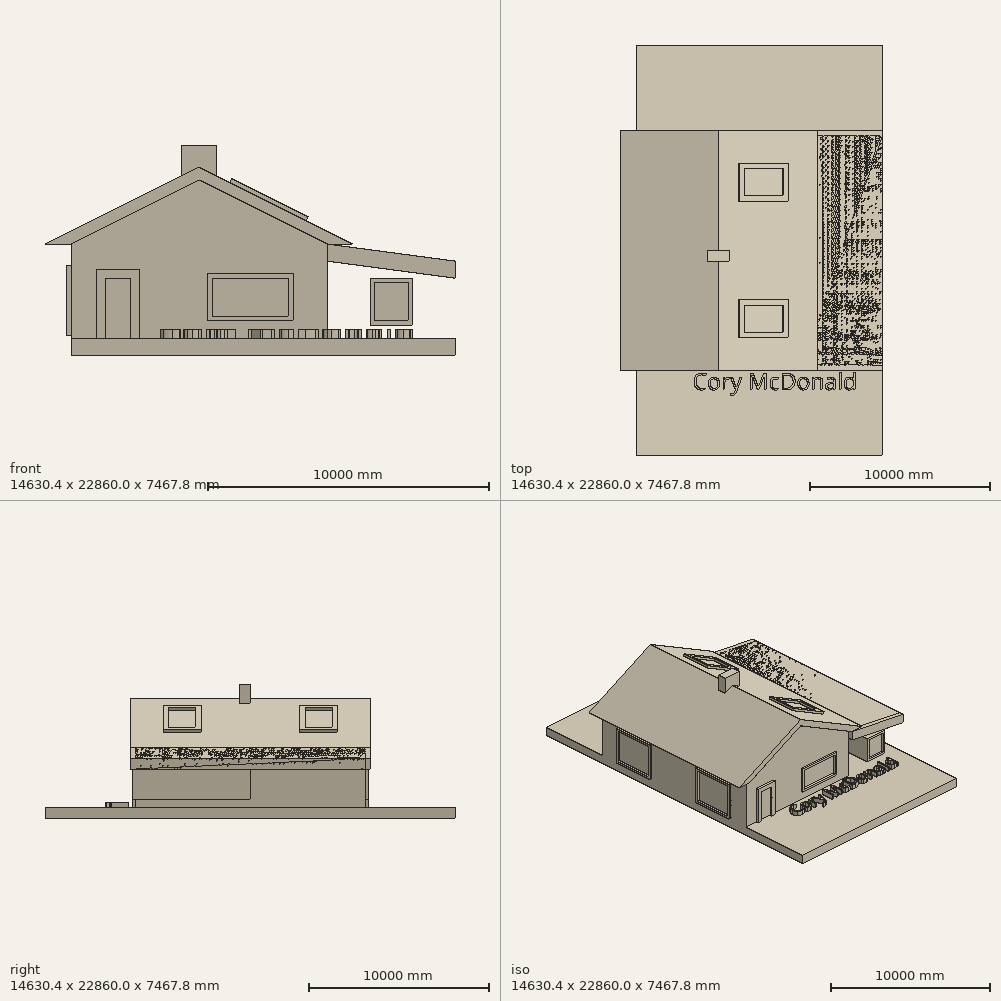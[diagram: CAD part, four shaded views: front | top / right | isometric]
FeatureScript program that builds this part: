
annotation { "Feature Type Name" : "Feature", "Feature Type Description" : "" }
export const myFeature = defineFeature(function(context is Context, id is Id, definition is map)
    precondition{}
    {
        {
            var Q0;
            Q0=qCreatedBy(makeId("Front.planeOp"),FACE);
            var sketch = newSketch(context, id + "F0", { "sketchPlane" : qUnion([Q0])});
            skLineSegment(sketch, "E0", {"start": v(0, 0) * mm, "end": v(-4572, 0) * mm});
            skLineSegment(sketch, "E1", {"start": v(0, 0) * mm, "end": v(4572, 0) * mm});
            skLineSegment(sketch, "E2", {"start": v(0, 0) * mm, "end": v(0, 2286) * mm});
            skLineSegment(sketch, "E3", {"start": v(0, 2286) * mm, "end": v(4572, 0) * mm});
            skLineSegment(sketch, "E4", {"start": v(0, 2286) * mm, "end": v(-4572, 0) * mm});
            skLineSegment(sketch, "E5", {"start": v(-4572, 0) * mm, "end": v(-5486.4, 0) * mm});
            skLineSegment(sketch, "E6", {"start": v(4572, 0) * mm, "end": v(5486.4, 0) * mm});
            skLineSegment(sketch, "E7", {"start": v(0, 2286) * mm, "end": v(0, 2743.2) * mm});
            skLineSegment(sketch, "E8", {"start": v(0, 2743.2) * mm, "end": v(-5486.4, 0) * mm});
            skLineSegment(sketch, "E9", {"start": v(0, 2743.2) * mm, "end": v(5486.4, 0) * mm});
            skLineSegment(sketch, "E10", {"start": v(-4572, 0) * mm, "end": v(-4572, -3352.8) * mm});
            skLineSegment(sketch, "E11", {"start": v(-4572, -3352.8) * mm, "end": v(4572, -3352.8) * mm});
            skLineSegment(sketch, "E12", {"start": v(4572, 0) * mm, "end": v(4572, -3352.8) * mm});
            skLineSegment(sketch, "E13", {"start": v(4572, -3352.8) * mm, "end": v(4572, -3962.4) * mm});
            skLineSegment(sketch, "E14", {"start": v(-4572, -3352.8) * mm, "end": v(-4572, -3962.4) * mm});
            skLineSegment(sketch, "E15", {"start": v(-4572, -3962.4) * mm, "end": v(4572, -3962.4) * mm});
            skLineSegment(sketch, "E16", {"start": v(4572, -3352.8) * mm, "end": v(9144, -3352.8) * mm});
            skLineSegment(sketch, "E17", {"start": v(4572, -3962.4) * mm, "end": v(9144, -3962.4) * mm});
            skLineSegment(sketch, "E18", {"start": v(9144, -3352.8) * mm, "end": v(9144, -3962.4) * mm});
            skLineSegment(sketch, "E19", {"start": v(9144, -3352.8) * mm, "end": v(9144, -609.6) * mm});
            skLineSegment(sketch, "E20", {"start": v(4572, 0) * mm, "end": v(9144, -609.6) * mm});
            skLineSegment(sketch, "E21", {"start": v(4572, 0) * mm, "end": v(4572, -609.6) * mm});
            skLineSegment(sketch, "E22", {"start": v(9144, -609.6) * mm, "end": v(9144, -1219.2) * mm});
            skLineSegment(sketch, "E23", {"start": v(9144, -1219.2) * mm, "end": v(4572, -609.6) * mm});
            skLineSegment(sketch, "E24", {"start": v(-3352.8, -3352.8) * mm, "end": v(-3352.8, -1219.2) * mm});
            skLineSegment(sketch, "E25", {"start": v(-3352.8, -1219.2) * mm, "end": v(-2438.4, -1219.2) * mm});
            skLineSegment(sketch, "E26", {"start": v(-2438.4, -1219.2) * mm, "end": v(-2438.4, -3352.8) * mm});
            skLineSegment(sketch, "E27.0", {"start": v(-2133.6, -914.4) * mm, "end": v(-2133.6, -3352.8) * mm});
            skLineSegment(sketch, "E27.1", {"start": v(-3657.6, -914.4) * mm, "end": v(-2133.6, -914.4) * mm});
            skLineSegment(sketch, "E27.2", {"start": v(-3657.6, -3352.8) * mm, "end": v(-3657.6, -914.4) * mm});
            skLineSegment(sketch, "E28.bottom", {"start": v(457.2, -1219.2) * mm, "end": v(3200.4, -1219.2) * mm});
            skLineSegment(sketch, "E28.top", {"start": v(457.2, -2590.8) * mm, "end": v(3200.4, -2590.8) * mm});
            skLineSegment(sketch, "E28.left", {"start": v(457.2, -1219.2) * mm, "end": v(457.2, -2590.8) * mm});
            skLineSegment(sketch, "E28.right", {"start": v(3200.4, -1219.2) * mm, "end": v(3200.4, -2590.8) * mm});
            skLineSegment(sketch, "E29.0", {"start": v(304.8, -1066.8) * mm, "end": v(3352.8, -1066.8) * mm});
            skLineSegment(sketch, "E29.1", {"start": v(304.8, -1066.8) * mm, "end": v(304.8, -2743.2) * mm});
            skLineSegment(sketch, "E29.2", {"start": v(304.8, -2743.2) * mm, "end": v(3352.8, -2743.2) * mm});
            skLineSegment(sketch, "E29.3", {"start": v(3352.8, -1066.8) * mm, "end": v(3352.8, -2743.2) * mm});
            skLineSegment(sketch, "E30.bottom", {"start": v(7467.6, -1371.6) * mm, "end": v(6248.4, -1371.6) * mm});
            skLineSegment(sketch, "E30.top", {"start": v(7467.6, -2743.2) * mm, "end": v(6248.4, -2743.2) * mm});
            skLineSegment(sketch, "E30.left", {"start": v(7467.6, -1371.6) * mm, "end": v(7467.6, -2743.2) * mm});
            skLineSegment(sketch, "E30.right", {"start": v(6248.4, -1371.6) * mm, "end": v(6248.4, -2743.2) * mm});
            skLineSegment(sketch, "E31.0", {"start": v(7620, -1219.2) * mm, "end": v(6096, -1219.2) * mm});
            skLineSegment(sketch, "E31.1", {"start": v(7620, -1219.2) * mm, "end": v(7620, -2895.6) * mm});
            skLineSegment(sketch, "E31.2", {"start": v(7620, -2895.6) * mm, "end": v(6096, -2895.6) * mm});
            skLineSegment(sketch, "E31.3", {"start": v(6096, -1219.2) * mm, "end": v(6096, -2895.6) * mm});
            skLineSegment(sketch, "E32", {"start": v(616.03, 2435.19) * mm, "end": v(616.03, 3505.35) * mm});
            skLineSegment(sketch, "E33", {"start": v(616.03, 3505.35) * mm, "end": v(-641, 3505.35) * mm});
            skLineSegment(sketch, "E34", {"start": v(-641, 3505.35) * mm, "end": v(-641, 2422.7) * mm});
            skSolve(sketch);
        }
        {
            var Q0;
            Q0=makeQuery(id+"F0.imprint","IMPRINT",FACE,{"disambiguationData":[TD([[makeQuery(id+"F0.imprint","IMPRINT",EDGE,{"derivedFrom":sQuery(id+"F0.wireOp",EDGE,"E3")}),1.0]])]});
            var Q1;
            Q1=makeQuery(id+"F0.imprint","IMPRINT",FACE,{"disambiguationData":[TD([[makeQuery(id+"F0.imprint","IMPRINT",EDGE,{"derivedFrom":sQuery(id+"F0.wireOp",EDGE,"E4")}),-1.0]])]});
            var Q2;
            Q2=makeQuery(id+"F0.imprint","IMPRINT",FACE,{"disambiguationData":[TD([[makeQuery(id+"F0.imprint","IMPRINT",EDGE,{"derivedFrom":sQuery(id+"F0.wireOp",EDGE,"E20")}),-1.0]])]});
            extrude(context, id + "F1", {"entities" : qUnion([Q0, Q1, Q2]), "endBound" : BoundingType.SYMMETRIC, "depth" : 13411.2 * mm, "offsetDistance" : 30.48 * mm});
        }
        {
            var Q0;
            Q0=makeQuery(id+"F0.imprint","IMPRINT",FACE,{"disambiguationData":[TD([[makeQuery(id+"F0.imprint","IMPRINT",EDGE,{"derivedFrom":sQuery(id+"F0.wireOp",EDGE,"E0")}),-1.0]])]});
            var Q1;
            Q1=makeQuery(id+"F0.imprint","IMPRINT",FACE,{"disambiguationData":[TD([[makeQuery(id+"F0.imprint","IMPRINT",EDGE,{"derivedFrom":sQuery(id+"F0.wireOp",EDGE,"E1")}),1.0]])]});
            var Q2;
            Q2=makeQuery(id+"F0.imprint","IMPRINT",FACE,{"disambiguationData":[TD([[makeQuery(id+"F0.imprint","IMPRINT",EDGE,{"derivedFrom":sQuery(id+"F0.wireOp",EDGE,"E0")}),1.0]])]});
            var Q3;
            Q3=makeQuery(id+"F0.imprint","IMPRINT",FACE,{"disambiguationData":[TD([[makeQuery(id+"F0.imprint","IMPRINT",EDGE,{"derivedFrom":sQuery(id+"F0.wireOp",EDGE,"E12")}),1.0]])]});
            extrude(context, id + "F2", {"entities" : qUnion([Q0, Q1, Q2, Q3]), "endBound" : BoundingType.SYMMETRIC, "depth" : 12801.6 * mm, "offsetDistance" : 30.48 * mm});
        }
        {
            var Q0;
            Q0=makeQuery(id+"F0.imprint","IMPRINT",FACE,{"disambiguationData":[TD([[makeQuery(id+"F0.imprint","IMPRINT",EDGE,{"derivedFrom":sQuery(id+"F0.wireOp",EDGE,"E13")}),1.0]])]});
            var Q1;
            {var subQ6=sQuery(id+"F0.wireOp",EDGE,"E13");Q1=makeQuery(id+"F0.imprint","IMPRINT",FACE,{"disambiguationData":[TD([[makeQuery(id+"F0.imprint","IMPRINT",EDGE,{"derivedFrom":subQ6}),-1.0]])]});}
            extrude(context, id + "F3", {"entities" : qUnion([Q0, Q1]), "operationType" : NewBodyOperationType.ADD, "endBound" : BoundingType.SYMMETRIC, "depth" : 22860 * mm, "offsetDistance" : 30.48 * mm});
        }
        {
            var Q0;
            Q0=makeQuery(id+"F0.imprint","IMPRINT",FACE,{"disambiguationData":[TD([[makeQuery(id+"F0.imprint","IMPRINT",EDGE,{"derivedFrom":sQuery(id+"F0.wireOp",EDGE,"E30.bottom")}),1.0]])]});
            var Q1;
            Q1=makeQuery(id+"F0.imprint","IMPRINT",FACE,{"disambiguationData":[TD([[makeQuery(id+"F0.imprint","IMPRINT",EDGE,{"derivedFrom":sQuery(id+"F0.wireOp",EDGE,"E28.bottom")}),-1.0]])]});
            extrude(context, id + "F4", {"entities" : qUnion([Q0, Q1]), "depth" : 6400.8 * mm, "offsetDistance" : 30.48 * mm});
        }
        {
            var Q0;
            Q0=makeQuery(id+"F0.imprint","IMPRINT",FACE,{"disambiguationData":[TD([[makeQuery(id+"F0.imprint","IMPRINT",EDGE,{"derivedFrom":sQuery(id+"F0.wireOp",EDGE,"E28.bottom")}),1.0]])]});
            var Q1;
            Q1=makeQuery(id+"F0.imprint","IMPRINT",FACE,{"disambiguationData":[TD([[makeQuery(id+"F0.imprint","IMPRINT",EDGE,{"derivedFrom":sQuery(id+"F0.wireOp",EDGE,"E30.bottom")}),-1.0]])]});
            extrude(context, id + "F5", {"entities" : qUnion([Q0, Q1]), "depth" : 6553.2 * mm, "offsetDistance" : 30.48 * mm});
        }
        {
            var Q0;
            {var subQ0=sQuery(id+"F0.wireOp",EDGE,"E24");Q0=makeQuery(id+"F0.imprint","IMPRINT",FACE,{"disambiguationData":[TD([[makeQuery(id+"F0.imprint","IMPRINT",EDGE,{"derivedFrom":subQ0}),1.0]])]});}
            extrude(context, id + "F6", {"entities" : qUnion([Q0]), "operationType" : NewBodyOperationType.ADD, "endBound" : BoundingType.SYMMETRIC, "depth" : 13106.4 * mm, "offsetDistance" : 30.48 * mm});
        }
        {
            var Q0;
            {var subQ0=sQuery(id+"F0.wireOp",EDGE,"E24");Q0=makeQuery(id+"F0.imprint","IMPRINT",FACE,{"disambiguationData":[TD([[makeQuery(id+"F0.imprint","IMPRINT",EDGE,{"derivedFrom":subQ0}),-1.0]])]});}
            extrude(context, id + "F7", {"entities" : qUnion([Q0]), "operationType" : NewBodyOperationType.ADD, "endBound" : BoundingType.SYMMETRIC, "depth" : 12801.6 * mm, "offsetDistance" : 30.48 * mm});
        }
        {
            var Q0;
            Q0=makeQuery(id+"F2.opExtrude","CAP_FACE",FACE,{"disambiguationData":[OSD([sQuery(id+"F0.wireOp",EDGE,"E3"),sQuery(id+"F0.wireOp",EDGE,"E4"),sQuery(id+"F0.wireOp",EDGE,"E10"),sQuery(id+"F0.wireOp",EDGE,"E11"),sQuery(id+"F0.wireOp",EDGE,"E16"),sQuery(id+"F0.wireOp",EDGE,"E19"),sQuery(id+"F0.wireOp",EDGE,"E21"),sQuery(id+"F0.wireOp",EDGE,"E23"),sQuery(id+"F0.wireOp",EDGE,"E27.0"),sQuery(id+"F0.wireOp",EDGE,"E27.1"),sQuery(id+"F0.wireOp",EDGE,"E27.2"),sQuery(id+"F0.wireOp",EDGE,"E29.0"),sQuery(id+"F0.wireOp",EDGE,"E29.1"),sQuery(id+"F0.wireOp",EDGE,"E29.2"),sQuery(id+"F0.wireOp",EDGE,"E29.3"),sQuery(id+"F0.wireOp",EDGE,"E31.0"),sQuery(id+"F0.wireOp",EDGE,"E31.1"),sQuery(id+"F0.wireOp",EDGE,"E31.2"),sQuery(id+"F0.wireOp",EDGE,"E31.3")])],"isStart":true});
            var sketch = newSketch(context, id + "F8", { "sketchPlane" : qUnion([Q0])});
            skLineSegment(sketch, "E35.bottom", {"start": v(-7620, -1219.2) * mm, "end": v(-6096, -1219.2) * mm});
            skLineSegment(sketch, "E35.top", {"start": v(-7620, -2895.6) * mm, "end": v(-6096, -2895.6) * mm});
            skLineSegment(sketch, "E35.left", {"start": v(-7620, -1219.2) * mm, "end": v(-7620, -2895.6) * mm});
            skLineSegment(sketch, "E35.right", {"start": v(-6096, -1219.2) * mm, "end": v(-6096, -2895.6) * mm});
            skLineSegment(sketch, "E36.0", {"start": v(-7315.2, -1524) * mm, "end": v(-6400.8, -1524) * mm});
            skLineSegment(sketch, "E36.1", {"start": v(-7315.2, -1524) * mm, "end": v(-7315.2, -2590.8) * mm});
            skLineSegment(sketch, "E36.2", {"start": v(-7315.2, -2590.8) * mm, "end": v(-6400.8, -2590.8) * mm});
            skLineSegment(sketch, "E36.3", {"start": v(-6400.8, -1524) * mm, "end": v(-6400.8, -2590.8) * mm});
            skSolve(sketch);
        }
        {
            var Q0;
            Q0 = qSketchRegion(id + "F8", true);
            extrude(context, id + "F9", {"entities" : qUnion([Q0]), "oppositeDirection" : true, "depth" : -3.05 * mm, "offsetDistance" : 30.48 * mm});
        }
        {
            var Q0;
            Q0=makeQuery(id+"F4.opExtrude","CAP_FACE",FACE,{"disambiguationData":[OSD([sQuery(id+"F0.wireOp",EDGE,"E28.bottom"),sQuery(id+"F0.wireOp",EDGE,"E28.top"),sQuery(id+"F0.wireOp",EDGE,"E28.left"),sQuery(id+"F0.wireOp",EDGE,"E28.right")])],"isStart":true});
            extrude(context, id + "F10", {"entities" : qUnion([Q0]), "operationType" : NewBodyOperationType.ADD, "depth" : 6400.8 * mm, "offsetDistance" : 30.48 * mm});
        }
        {
            var Q0;
            Q0=makeQuery(id+"F5.opExtrude","CAP_FACE",FACE,{"disambiguationData":[OSD([sQuery(id+"F0.wireOp",EDGE,"E28.bottom"),sQuery(id+"F0.wireOp",EDGE,"E28.top"),sQuery(id+"F0.wireOp",EDGE,"E28.left"),sQuery(id+"F0.wireOp",EDGE,"E28.right"),sQuery(id+"F0.wireOp",EDGE,"E29.0"),sQuery(id+"F0.wireOp",EDGE,"E29.1"),sQuery(id+"F0.wireOp",EDGE,"E29.2"),sQuery(id+"F0.wireOp",EDGE,"E29.3")])],"isStart":true});
            extrude(context, id + "F11", {"entities" : qUnion([Q0]), "depth" : 6553.2 * mm, "offsetDistance" : 30.48 * mm});
        }
        {
            var Q0;
            Q0 = qSketchRegion(id + "F8", true);
            extrude(context, id + "F12", {"entities" : qUnion([Q0]), "operationType" : NewBodyOperationType.ADD, "depth" : 152.4 * mm, "offsetDistance" : 30.48 * mm});
        }
        {
            var Q0;
            Q0=makeQuery(id+"F8.imprint","IMPRINT",FACE,{"disambiguationData":[TD([[makeQuery(id+"F8.imprint","IMPRINT",EDGE,{"derivedFrom":sQuery(id+"F8.wireOp",EDGE,"E36.0")}),-1.0]])]});
            extrude(context, id + "F13", {"entities" : qUnion([Q0]), "operationType" : NewBodyOperationType.ADD, "depth" : 30.48 * mm, "offsetDistance" : 30.48 * mm});
        }
        {
            var Q0;
            Q0=makeQuery(id+"F1.opExtrude","SWEPT_FACE",FACE,{"disambiguationData":[OSD([sQuery(id+"F0.wireOp",EDGE,"E9")])]});
            var sketch = newSketch(context, id + "F14", { "sketchPlane" : qUnion([Q0])});
            skLineSegment(sketch, "E37.bottom", {"start": v(-7.6, -4876.8) * mm, "end": v(3040.4, -4876.8) * mm});
            skLineSegment(sketch, "E37.top", {"start": v(-7.6, -2743.2) * mm, "end": v(3040.4, -2743.2) * mm});
            skLineSegment(sketch, "E37.left", {"start": v(-7.6, -4876.8) * mm, "end": v(-7.6, -2743.2) * mm});
            skLineSegment(sketch, "E37.right", {"start": v(3040.4, -4876.8) * mm, "end": v(3040.4, -2743.2) * mm});
            skLineSegment(sketch, "E38.bottom", {"start": v(-7.6, 2743.2) * mm, "end": v(3040.4, 2743.2) * mm});
            skLineSegment(sketch, "E38.top", {"start": v(-7.6, 4876.8) * mm, "end": v(3040.4, 4876.8) * mm});
            skLineSegment(sketch, "E38.left", {"start": v(-7.6, 2743.2) * mm, "end": v(-7.6, 4876.8) * mm});
            skLineSegment(sketch, "E38.right", {"start": v(3040.4, 2743.2) * mm, "end": v(3040.4, 4876.8) * mm});
            skLineSegment(sketch, "E39.0", {"start": v(297.2, -3048) * mm, "end": v(2735.6, -3048) * mm});
            skLineSegment(sketch, "E39.1", {"start": v(297.2, -4572) * mm, "end": v(297.2, -3048) * mm});
            skLineSegment(sketch, "E39.2", {"start": v(297.2, -4572) * mm, "end": v(2735.6, -4572) * mm});
            skLineSegment(sketch, "E39.3", {"start": v(2735.6, -4572) * mm, "end": v(2735.6, -3048) * mm});
            skLineSegment(sketch, "E40.0", {"start": v(297.2, 3048) * mm, "end": v(297.2, 4572) * mm});
            skLineSegment(sketch, "E40.1", {"start": v(297.2, 3048) * mm, "end": v(2735.6, 3048) * mm});
            skLineSegment(sketch, "E40.2", {"start": v(2735.6, 3048) * mm, "end": v(2735.6, 4572) * mm});
            skLineSegment(sketch, "E40.3", {"start": v(297.2, 4572) * mm, "end": v(2735.6, 4572) * mm});
            skSolve(sketch);
        }
        {
            var Q0;
            Q0=makeQuery(id+"F14.imprint","IMPRINT",FACE,{"disambiguationData":[TD([[makeQuery(id+"F14.imprint","IMPRINT",EDGE,{"derivedFrom":sQuery(id+"F14.wireOp",EDGE,"E38.bottom")}),1.0]])]});
            var Q1;
            Q1=makeQuery(id+"F14.imprint","IMPRINT",FACE,{"disambiguationData":[TD([[makeQuery(id+"F14.imprint","IMPRINT",EDGE,{"derivedFrom":sQuery(id+"F14.wireOp",EDGE,"E37.bottom")}),1.0]])]});
            extrude(context, id + "F15", {"entities" : qUnion([Q0, Q1]), "operationType" : NewBodyOperationType.ADD, "depth" : 152.4 * mm, "offsetDistance" : 30.48 * mm});
        }
        {
            var Q0;
            Q0=makeQuery(id+"F3.boolean.opBoolean","MERGE",FACE,{"derivedFrom":[makeQuery(id+"F2.opExtrude","SWEPT_FACE",FACE,{"disambiguationData":[OSD([sQuery(id+"F0.wireOp",EDGE,"E10")])]}),makeQuery(id+"F3.opExtrude","SWEPT_FACE",FACE,{"disambiguationData":[OSD([sQuery(id+"F0.wireOp",EDGE,"E14")])]})]});
            var sketch = newSketch(context, id + "F16", { "sketchPlane" : qUnion([Q0])});
            skLineSegment(sketch, "E41.bottom", {"start": v(-4876.8, -914.4) * mm, "end": v(-2190.3, -914.4) * mm});
            skLineSegment(sketch, "E41.top", {"start": v(-4876.8, -3122.77) * mm, "end": v(-2190.3, -3122.77) * mm});
            skLineSegment(sketch, "E41.left", {"start": v(-4876.8, -914.4) * mm, "end": v(-4876.8, -3122.77) * mm});
            skLineSegment(sketch, "E41.right", {"start": v(-2190.3, -914.4) * mm, "end": v(-2190.3, -3122.77) * mm});
            skLineSegment(sketch, "E42.bottom", {"start": v(2190.19, -914.4) * mm, "end": v(4876.8, -914.4) * mm});
            skLineSegment(sketch, "E42.top", {"start": v(2190.19, -3122.68) * mm, "end": v(4876.8, -3122.68) * mm});
            skLineSegment(sketch, "E42.left", {"start": v(2190.19, -914.4) * mm, "end": v(2190.19, -3122.68) * mm});
            skLineSegment(sketch, "E42.right", {"start": v(4876.8, -914.4) * mm, "end": v(4876.8, -3122.68) * mm});
            skLineSegment(sketch, "E43.0", {"start": v(2037.79, -762) * mm, "end": v(5029.2, -762) * mm});
            skLineSegment(sketch, "E43.1", {"start": v(2037.79, -762) * mm, "end": v(2037.79, -3275.08) * mm});
            skLineSegment(sketch, "E43.2", {"start": v(2037.79, -3275.08) * mm, "end": v(5029.2, -3275.08) * mm});
            skLineSegment(sketch, "E43.3", {"start": v(5029.2, -762) * mm, "end": v(5029.2, -3275.08) * mm});
            skLineSegment(sketch, "E44.0", {"start": v(-5029.2, -762) * mm, "end": v(-2037.9, -762) * mm});
            skLineSegment(sketch, "E44.1", {"start": v(-5029.2, -762) * mm, "end": v(-5029.2, -3275.17) * mm});
            skLineSegment(sketch, "E44.2", {"start": v(-5029.2, -3275.17) * mm, "end": v(-2037.9, -3275.17) * mm});
            skLineSegment(sketch, "E44.3", {"start": v(-2037.9, -762) * mm, "end": v(-2037.9, -3275.17) * mm});
            skSolve(sketch);
        }
        {
            var Q0;
            Q0=makeQuery(id+"F16.imprint","IMPRINT",FACE,{"disambiguationData":[TD([[makeQuery(id+"F16.imprint","IMPRINT",EDGE,{"derivedFrom":sQuery(id+"F16.wireOp",EDGE,"E42.bottom")}),1.0]])]});
            var Q1;
            Q1=makeQuery(id+"F16.imprint","IMPRINT",FACE,{"disambiguationData":[TD([[makeQuery(id+"F16.imprint","IMPRINT",EDGE,{"derivedFrom":sQuery(id+"F16.wireOp",EDGE,"E41.bottom")}),1.0]])]});
            extrude(context, id + "F17", {"entities" : qUnion([Q0, Q1]), "operationType" : NewBodyOperationType.ADD, "depth" : 152.4 * mm, "offsetDistance" : 30.48 * mm});
        }
        {
            var Q0;
            {var subQ0=sQuery(id+"F0.wireOp",EDGE,"E32");Q0=makeQuery(id+"F0.imprint","IMPRINT",FACE,{"disambiguationData":[TD([[makeQuery(id+"F0.imprint","IMPRINT",EDGE,{"derivedFrom":subQ0}),1.0]])]});}
            extrude(context, id + "F18", {"entities" : qUnion([Q0]), "operationType" : NewBodyOperationType.ADD, "depth" : 609.6 * mm, "offsetDistance" : 30.48 * mm});
        }
        {
            var Q0;
            {var subQ3=sQuery(id+"F0.wireOp",EDGE,"E26");var subQ4=sQuery(id+"F0.wireOp",EDGE,"E25");var subQ5=sQuery(id+"F0.wireOp",EDGE,"E24");var subQ6=sQuery(id+"F0.wireOp",EDGE,"E11");var subQ9=sQuery(id+"F0.wireOp",EDGE,"E16");Q0=makeQuery(id+"F7.boolean.opBoolean","SPLIT",FACE,{"disambiguationData":[TD([makeQuery(id+"F7.opExtrude","CAP_FACE",FACE,{"disambiguationData":[OSD([subQ6,subQ5,subQ4,subQ3])],"isStart":false})])],"derivedFrom":makeQuery(id+"F3.opExtrude","SWEPT_FACE",FACE,{"disambiguationData":[OSD([subQ6,subQ9])]})});}
            var sketch = newSketch(context, id + "F19", { "sketchPlane" : qUnion([Q0])});
            skText(sketch, "E45", { "text": "Cory McDonald", "fontName": "OpenSans-Regular.ttf"});
            const initialGuessF19  = {"E45": [-1.44748, -7.7724, 1, 0, 0.92291]};
            skSetInitialGuess(sketch, initialGuessF19);
            skSolve(sketch);
        }
        {
            var Q0;
            Q0 = qSketchRegion(id + "F19", true);
            extrude(context, id + "F20", {"entities" : qUnion([Q0]), "operationType" : NewBodyOperationType.ADD, "depth" : 304.8 * mm, "offsetDistance" : 30.48 * mm});
        }
    });
